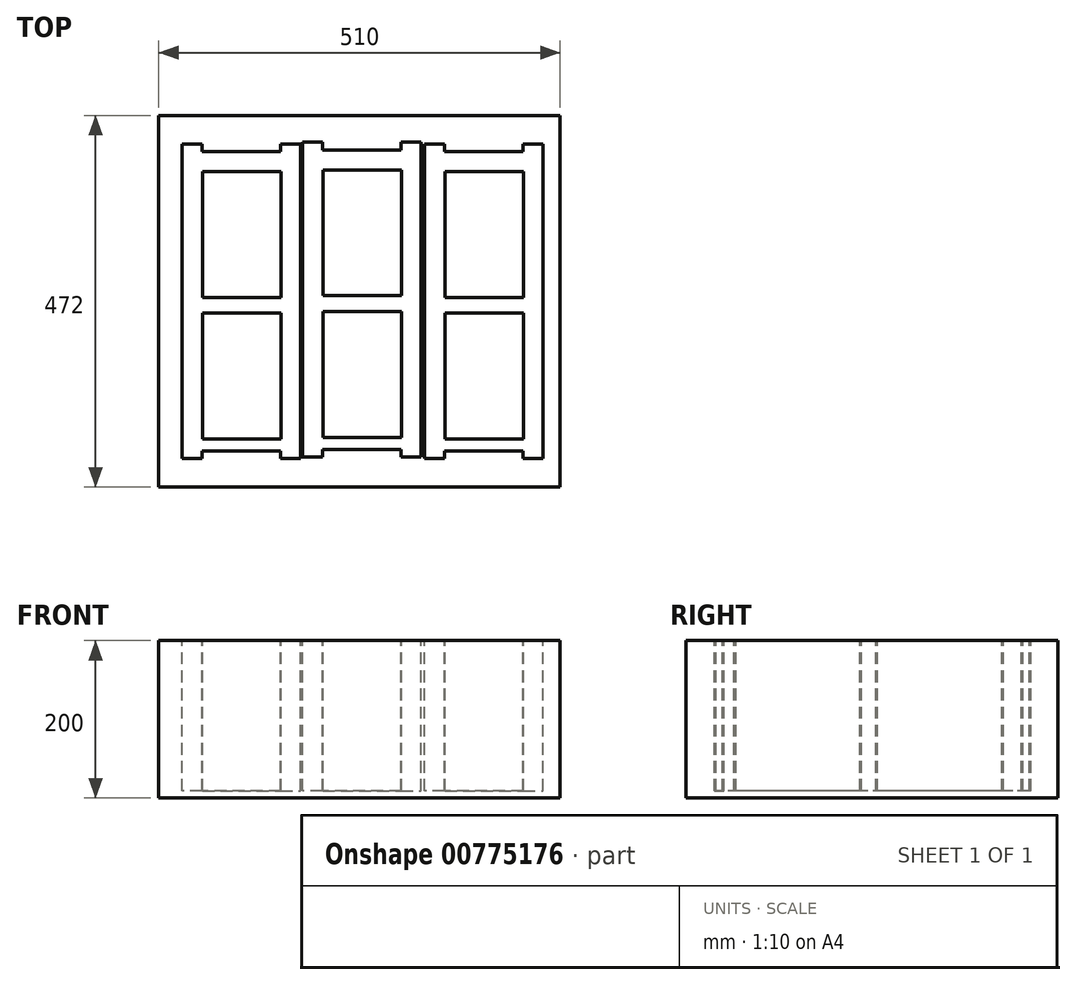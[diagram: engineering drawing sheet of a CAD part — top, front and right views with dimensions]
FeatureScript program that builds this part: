
annotation { "Feature Type Name" : "Feature", "Feature Type Description" : "" }
export const myFeature = defineFeature(function(context is Context, id is Id, definition is map)
    precondition{}
    {
        {
            var Q0;
            Q0=qCreatedBy(makeId("Top.planeOp"),FACE);
            var sketch = newSketch(context, id + "F0", { "sketchPlane" : qUnion([Q0])});
            skLineSegment(sketch, "E0.bottom", {"start": v(-316.29, 209.58) * mm, "end": v(193.71, 209.58) * mm});
            skLineSegment(sketch, "E0.top", {"start": v(-316.29, -262.42) * mm, "end": v(193.71, -262.42) * mm});
            skLineSegment(sketch, "E0.left", {"start": v(-316.29, 209.58) * mm, "end": v(-316.29, -262.42) * mm});
            skLineSegment(sketch, "E0.right", {"start": v(193.71, 209.58) * mm, "end": v(193.71, -262.42) * mm});
            skSolve(sketch);
        }
        {
            var Q0;
            Q0=makeQuery(id+"F0.imprint","IMPRINT",FACE,{"disambiguationData":[TD([[makeQuery(id+"F0.imprint","IMPRINT",EDGE,{"derivedFrom":sQuery(id+"F0.wireOp",EDGE,"E0.bottom")}),-1.0]])]});
            extrude(context, id + "F1", {"entities" : qUnion([Q0]), "depth" : 200 * mm, "offsetDistance" : 25 * mm});
        }
        {
            var Q0;
            Q0=makeQuery(id+"F1.opExtrude","CAP_FACE",FACE,{"disambiguationData":[OSD([sQuery(id+"F0.wireOp",EDGE,"E0.bottom"),sQuery(id+"F0.wireOp",EDGE,"E0.top"),sQuery(id+"F0.wireOp",EDGE,"E0.left"),sQuery(id+"F0.wireOp",EDGE,"E0.right")])],"isStart":false});
            var sketch = newSketch(context, id + "F2", { "sketchPlane" : qUnion([Q0])});
            skLineSegment(sketch, "E1", {"start": v(-286.29, 173.58) * mm, "end": v(-286.29, -226.42) * mm});
            skLineSegment(sketch, "E2", {"start": v(-286.29, -226.42) * mm, "end": v(-261.29, -226.42) * mm});
            skLineSegment(sketch, "E3", {"start": v(-261.29, -226.42) * mm, "end": v(-261.29, -216.42) * mm});
            skLineSegment(sketch, "E4", {"start": v(-261.29, -216.42) * mm, "end": v(-161.29, -216.42) * mm});
            skLineSegment(sketch, "E5", {"start": v(-161.29, -216.42) * mm, "end": v(-161.29, -226.42) * mm});
            skLineSegment(sketch, "E6", {"start": v(-161.29, -226.42) * mm, "end": v(-136.29, -226.42) * mm});
            skLineSegment(sketch, "E7", {"start": v(-136.29, -226.42) * mm, "end": v(-136.29, 173.58) * mm});
            skLineSegment(sketch, "E8", {"start": v(-161.29, 173.58) * mm, "end": v(-161.29, 163.58) * mm});
            skLineSegment(sketch, "E9", {"start": v(-161.29, 163.58) * mm, "end": v(-261.29, 163.58) * mm});
            skLineSegment(sketch, "E10", {"start": v(-261.29, 163.58) * mm, "end": v(-261.29, 173.58) * mm});
            skLineSegment(sketch, "E11", {"start": v(-261.29, 173.58) * mm, "end": v(-286.29, 173.58) * mm});
            skLineSegment(sketch, "E12", {"start": v(-136.29, 173.58) * mm, "end": v(-161.29, 173.58) * mm});
            skLineSegment(sketch, "E13.bottom", {"start": v(-260.73, 138.59) * mm, "end": v(-160.73, 138.59) * mm});
            skLineSegment(sketch, "E13.top", {"start": v(-260.73, -21.41) * mm, "end": v(-160.73, -21.41) * mm});
            skLineSegment(sketch, "E13.left", {"start": v(-260.73, 138.59) * mm, "end": v(-260.73, -21.41) * mm});
            skLineSegment(sketch, "E13.right", {"start": v(-160.73, 138.59) * mm, "end": v(-160.73, -21.41) * mm});
            skLineSegment(sketch, "E14.bottom", {"start": v(-260.6, -41.43) * mm, "end": v(-160.6, -41.43) * mm});
            skLineSegment(sketch, "E14.top", {"start": v(-260.6, -201.43) * mm, "end": v(-160.6, -201.43) * mm});
            skLineSegment(sketch, "E14.left", {"start": v(-260.6, -41.43) * mm, "end": v(-260.6, -201.43) * mm});
            skLineSegment(sketch, "E14.right", {"start": v(-160.6, -41.43) * mm, "end": v(-160.6, -201.43) * mm});
            skSolve(sketch);
        }
        {
            var Q0;
            Q0=makeQuery(id+"F2.imprint","IMPRINT",FACE,{"disambiguationData":[TD([[makeQuery(id+"F2.imprint","IMPRINT",EDGE,{"derivedFrom":sQuery(id+"F2.wireOp",EDGE,"E1")}),1.0]])]});
            extrude(context, id + "F3", {"entities" : qUnion([Q0]), "operationType" : NewBodyOperationType.REMOVE, "oppositeDirection" : true, "depth" : 191 * mm, "offsetDistance" : 25 * mm});
        }
        {
            var Q0;
            {var subQ0=sQuery(id+"F0.wireOp",EDGE,"E0.left");var subQ1=sQuery(id+"F0.wireOp",EDGE,"E0.bottom");var subQ2=sQuery(id+"F0.wireOp",EDGE,"E0.right");var subQ3=sQuery(id+"F0.wireOp",EDGE,"E0.top");Q0=makeQuery(id+"F3.boolean.opBoolean","SPLIT",FACE,{"disambiguationData":[TD([makeQuery(id+"F1.opExtrude","SWEPT_FACE",FACE,{"disambiguationData":[OSD([subQ1])]})])],"derivedFrom":makeQuery(id+"F1.opExtrude","CAP_FACE",FACE,{"disambiguationData":[OSD([subQ1,subQ3,subQ0,subQ2])],"isStart":false})});}
            var sketch = newSketch(context, id + "F4", { "sketchPlane" : qUnion([Q0])});
            skLineSegment(sketch, "E15", {"start": v(-133.29, 175.58) * mm, "end": v(-133.29, -224.42) * mm});
            skLineSegment(sketch, "E16", {"start": v(-133.29, -224.42) * mm, "end": v(-108.29, -224.42) * mm});
            skLineSegment(sketch, "E17", {"start": v(-108.29, -224.42) * mm, "end": v(-108.29, -214.42) * mm});
            skLineSegment(sketch, "E18", {"start": v(-108.29, -214.42) * mm, "end": v(-8.29, -214.42) * mm});
            skLineSegment(sketch, "E19", {"start": v(-8.29, -214.42) * mm, "end": v(-8.29, -224.42) * mm});
            skLineSegment(sketch, "E20", {"start": v(-8.29, -224.42) * mm, "end": v(16.71, -224.42) * mm});
            skLineSegment(sketch, "E21", {"start": v(16.71, -224.42) * mm, "end": v(16.71, 175.58) * mm});
            skLineSegment(sketch, "E22", {"start": v(-8.29, 175.58) * mm, "end": v(-8.29, 165.58) * mm});
            skLineSegment(sketch, "E23", {"start": v(-8.29, 165.58) * mm, "end": v(-108.29, 165.58) * mm});
            skLineSegment(sketch, "E24", {"start": v(-108.29, 165.58) * mm, "end": v(-108.29, 175.58) * mm});
            skLineSegment(sketch, "E25", {"start": v(-108.29, 175.58) * mm, "end": v(-133.29, 175.58) * mm});
            skLineSegment(sketch, "E26", {"start": v(16.71, 175.58) * mm, "end": v(-8.29, 175.58) * mm});
            skLineSegment(sketch, "E27.bottom", {"start": v(-107.73, 140.59) * mm, "end": v(-7.73, 140.59) * mm});
            skLineSegment(sketch, "E27.top", {"start": v(-107.73, -19.41) * mm, "end": v(-7.73, -19.41) * mm});
            skLineSegment(sketch, "E27.left", {"start": v(-107.73, 140.59) * mm, "end": v(-107.73, -19.41) * mm});
            skLineSegment(sketch, "E27.right", {"start": v(-7.73, 140.59) * mm, "end": v(-7.73, -19.41) * mm});
            skLineSegment(sketch, "E28.bottom", {"start": v(-107.6, -39.43) * mm, "end": v(-7.6, -39.43) * mm});
            skLineSegment(sketch, "E28.top", {"start": v(-107.6, -199.43) * mm, "end": v(-7.6, -199.43) * mm});
            skLineSegment(sketch, "E28.left", {"start": v(-107.6, -39.43) * mm, "end": v(-107.6, -199.43) * mm});
            skLineSegment(sketch, "E28.right", {"start": v(-7.6, -39.43) * mm, "end": v(-7.6, -199.43) * mm});
            skSolve(sketch);
        }
        {
            var Q0;
            Q0 = qSketchRegion(id + "F4", true);
            extrude(context, id + "F5", {"entities" : qUnion([Q0]), "operationType" : NewBodyOperationType.REMOVE, "oppositeDirection" : true, "depth" : 191 * mm, "offsetDistance" : 25 * mm});
        }
        {
            var Q0;
            {var subQ5=sQuery(id+"F0.wireOp",EDGE,"E0.left");var subQ7=sQuery(id+"F0.wireOp",EDGE,"E0.top");var subQ9=sQuery(id+"F0.wireOp",EDGE,"E0.right");var subQ13=sQuery(id+"F0.wireOp",EDGE,"E0.bottom");var subQ14=makeQuery(id+"F1.opExtrude","SWEPT_FACE",FACE,{"disambiguationData":[OSD([subQ13])]});Q0=makeQuery(id+"F5.boolean.opBoolean","SPLIT",FACE,{"disambiguationData":[TD([subQ14])],"derivedFrom":makeQuery(id+"F3.boolean.opBoolean","SPLIT",FACE,{"disambiguationData":[TD([subQ14])],"derivedFrom":makeQuery(id+"F1.opExtrude","CAP_FACE",FACE,{"disambiguationData":[OSD([subQ13,subQ7,subQ5,subQ9])],"isStart":false})})});}
            var sketch = newSketch(context, id + "F6", { "sketchPlane" : qUnion([Q0])});
            skLineSegment(sketch, "E29", {"start": v(21.71, 173.58) * mm, "end": v(21.71, -226.42) * mm});
            skLineSegment(sketch, "E30", {"start": v(21.71, -226.42) * mm, "end": v(46.71, -226.42) * mm});
            skLineSegment(sketch, "E31", {"start": v(46.71, -226.42) * mm, "end": v(46.71, -216.42) * mm});
            skLineSegment(sketch, "E32", {"start": v(46.71, -216.42) * mm, "end": v(146.71, -216.42) * mm});
            skLineSegment(sketch, "E33", {"start": v(146.71, -216.42) * mm, "end": v(146.71, -226.42) * mm});
            skLineSegment(sketch, "E34", {"start": v(146.71, -226.42) * mm, "end": v(171.71, -226.42) * mm});
            skLineSegment(sketch, "E35", {"start": v(171.71, -226.42) * mm, "end": v(171.71, 173.58) * mm});
            skLineSegment(sketch, "E36", {"start": v(146.71, 173.58) * mm, "end": v(146.71, 163.58) * mm});
            skLineSegment(sketch, "E37", {"start": v(146.71, 163.58) * mm, "end": v(46.71, 163.58) * mm});
            skLineSegment(sketch, "E38", {"start": v(46.71, 163.58) * mm, "end": v(46.71, 173.58) * mm});
            skLineSegment(sketch, "E39", {"start": v(46.71, 173.58) * mm, "end": v(21.71, 173.58) * mm});
            skLineSegment(sketch, "E40", {"start": v(171.71, 173.58) * mm, "end": v(146.71, 173.58) * mm});
            skLineSegment(sketch, "E41.bottom", {"start": v(47.27, 138.59) * mm, "end": v(147.27, 138.59) * mm});
            skLineSegment(sketch, "E41.top", {"start": v(47.27, -21.41) * mm, "end": v(147.27, -21.41) * mm});
            skLineSegment(sketch, "E41.left", {"start": v(47.27, 138.59) * mm, "end": v(47.27, -21.41) * mm});
            skLineSegment(sketch, "E41.right", {"start": v(147.27, 138.59) * mm, "end": v(147.27, -21.41) * mm});
            skLineSegment(sketch, "E42.bottom", {"start": v(47.4, -41.43) * mm, "end": v(147.4, -41.43) * mm});
            skLineSegment(sketch, "E42.top", {"start": v(47.4, -201.43) * mm, "end": v(147.4, -201.43) * mm});
            skLineSegment(sketch, "E42.left", {"start": v(47.4, -41.43) * mm, "end": v(47.4, -201.43) * mm});
            skLineSegment(sketch, "E42.right", {"start": v(147.4, -41.43) * mm, "end": v(147.4, -201.43) * mm});
            skSolve(sketch);
        }
        {
            var Q0;
            Q0 = qSketchRegion(id + "F6", true);
            extrude(context, id + "F7", {"entities" : qUnion([Q0]), "operationType" : NewBodyOperationType.REMOVE, "oppositeDirection" : true, "depth" : 191 * mm, "offsetDistance" : 25 * mm});
        }
    });
